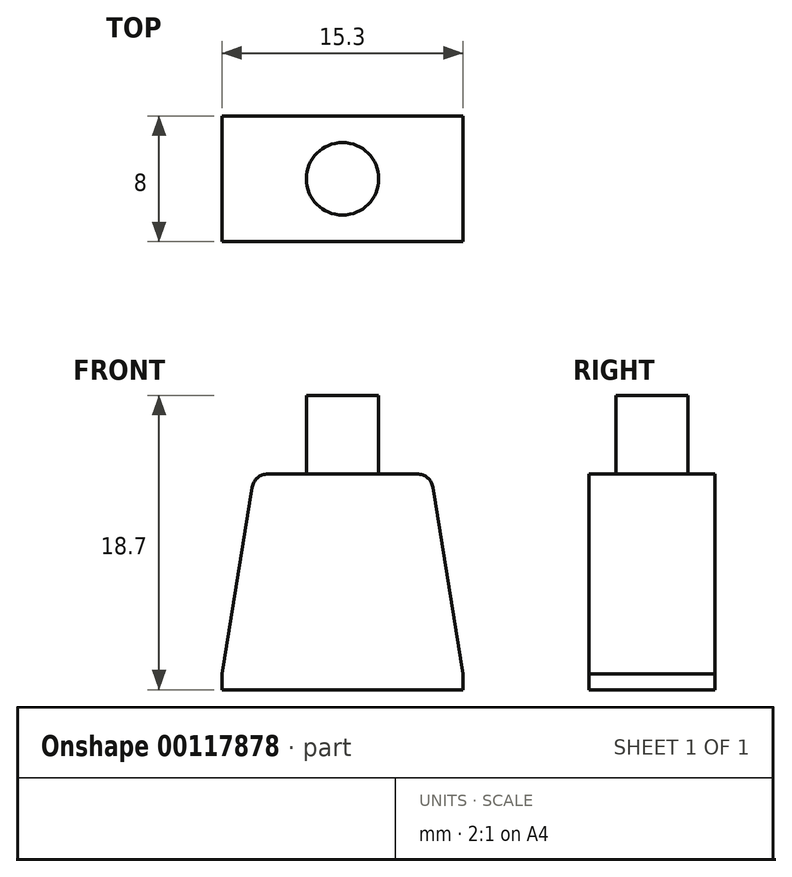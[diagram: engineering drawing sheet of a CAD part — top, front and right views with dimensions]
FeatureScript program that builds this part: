
annotation { "Feature Type Name" : "Feature", "Feature Type Description" : "" }
export const myFeature = defineFeature(function(context is Context, id is Id, definition is map)
    precondition{}
    {
        {
            var Q0;
            Q0=qCreatedBy(makeId("Front.planeOp"),FACE);
            var sketch = newSketch(context, id + "F0", { "sketchPlane" : qUnion([Q0])});
            skLineSegment(sketch, "E0", {"start": v(-7.65, 0) * mm, "end": v(7.65, 0) * mm});
            skLineSegment(sketch, "E1", {"start": v(7.65, 0) * mm, "end": v(7.65, 1) * mm});
            skLineSegment(sketch, "E2", {"start": v(7.65, 1) * mm, "end": v(5.74, 12.86) * mm});
            skLineSegment(sketch, "E3", {"start": v(4.75, 13.7) * mm, "end": v(-4.75, 13.7) * mm});
            skLineSegment(sketch, "E4", {"start": v(-5.74, 12.86) * mm, "end": v(-7.65, 1) * mm});
            skLineSegment(sketch, "E5", {"start": v(-7.65, 1) * mm, "end": v(-7.65, 0) * mm});
            skPoint(sketch, "E6.visualSharp", {"position": v(-5.6, 13.7) * mm});
            skArc(sketch, "E6.filletArc", {"start": v(-4.75, 13.7) * mm, "mid": v(-5.4, 13.46) * mm, "end": v(-5.74, 12.86) * mm});
            skPoint(sketch, "E7.visualSharp", {"position": v(5.6, 13.7) * mm});
            skArc(sketch, "E7.filletArc", {"start": v(5.74, 12.86) * mm, "mid": v(5.4, 13.46) * mm, "end": v(4.75, 13.7) * mm});
            skSolve(sketch);
        }
        {
            var Q0;
            Q0 = qSketchRegion(id + "F0", true);
            extrude(context, id + "F1", {"entities" : qUnion([Q0]), "endBound" : BoundingType.SYMMETRIC, "depth" : 8 * mm});
        }
        {
            var Q0;
            Q0=makeQuery(id+"F1.opExtrude","SWEPT_FACE",FACE,{"disambiguationData":[OSD([sQuery(id+"F0.wireOp",EDGE,"E3")])]});
            var sketch = newSketch(context, id + "F2", { "sketchPlane" : qUnion([Q0])});
            skCircle(sketch, "E8", {"center": v(0, 0) * mm, "radius": 2.3 * mm});
            skSolve(sketch);
        }
        {
            var Q0;
            Q0 = qSketchRegion(id + "F2", true);
            extrude(context, id + "F3", {"entities" : qUnion([Q0]), "operationType" : NewBodyOperationType.ADD, "depth" : 5 * mm});
        }
    });
